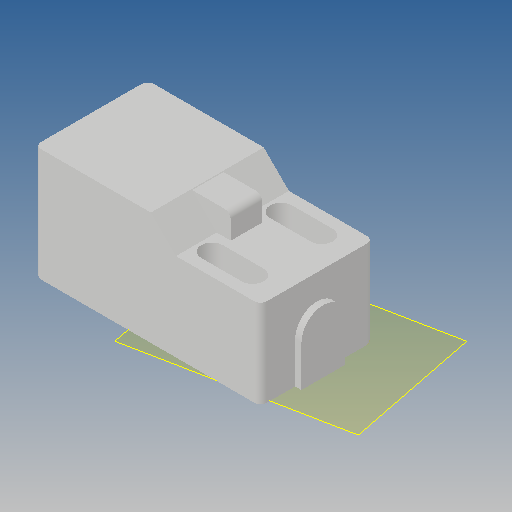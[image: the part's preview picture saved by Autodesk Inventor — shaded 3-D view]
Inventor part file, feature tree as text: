
AUTODESK INVENTOR PART (.ipt)
format: ipt  version: 2021 (Build 250183000, 183)  size: 150,528 bytes
history: native  units: mm
features: other x4, plane x1
ambient origin geometry x8: Origin, YZ Plane, XZ Plane, XY Plane, X Axis, Y Axis, Z Axis, Center Point
bodies: Solid1 (feature_tree)
feature tree (5):
  plane  "Work Plane1"
  other  "Âûðåç-Âûòÿíóòü3"
  other  "<userpath>\OneDrive\Objet3D\3DPrinter\3DPrinterBeltCoreXY.iam"
  other  "3DPrinterBeltCoreXY.iam"
  other  "HotendMountCarriage:1"
